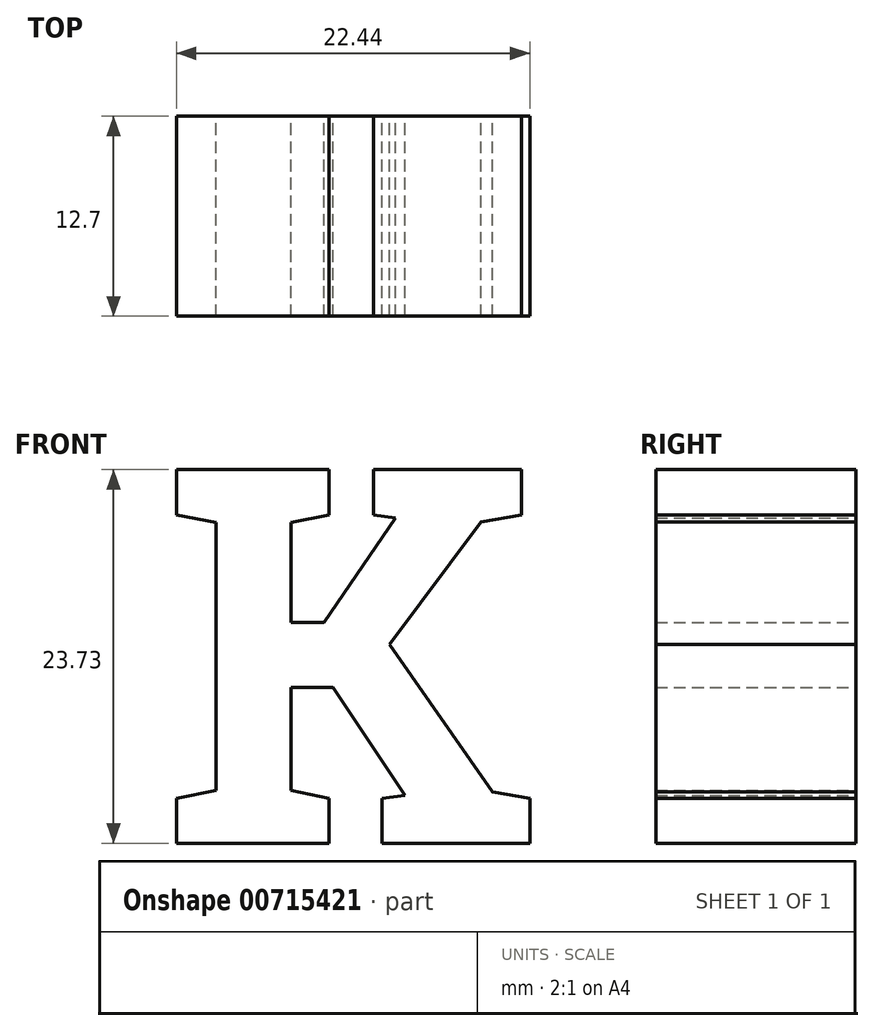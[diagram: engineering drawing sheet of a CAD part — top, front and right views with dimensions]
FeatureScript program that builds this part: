
annotation { "Feature Type Name" : "Feature", "Feature Type Description" : "" }
export const myFeature = defineFeature(function(context is Context, id is Id, definition is map)
    precondition{}
    {
        {
            var Q0;
            Q0=qCreatedBy(makeId("Front.planeOp"),FACE);
            var sketch = newSketch(context, id + "F0", { "sketchPlane" : qUnion([Q0])});
            skText(sketch, "E0", { "text": "K", "fontName": "RobotoSlab-Bold.ttf"});
            const initialGuessF0  = {"E0": [0, 0, 1, 0, 0.02403]};
            skSetInitialGuess(sketch, initialGuessF0);
            skSolve(sketch);
        }
        {
            var Q0;
            Q0 = qSketchRegion(id + "F0", true);
            extrude(context, id + "F1", {"entities" : qUnion([Q0]), "depth" : 12.7 * mm, "offsetDistance" : 25.4 * mm});
        }
    });
